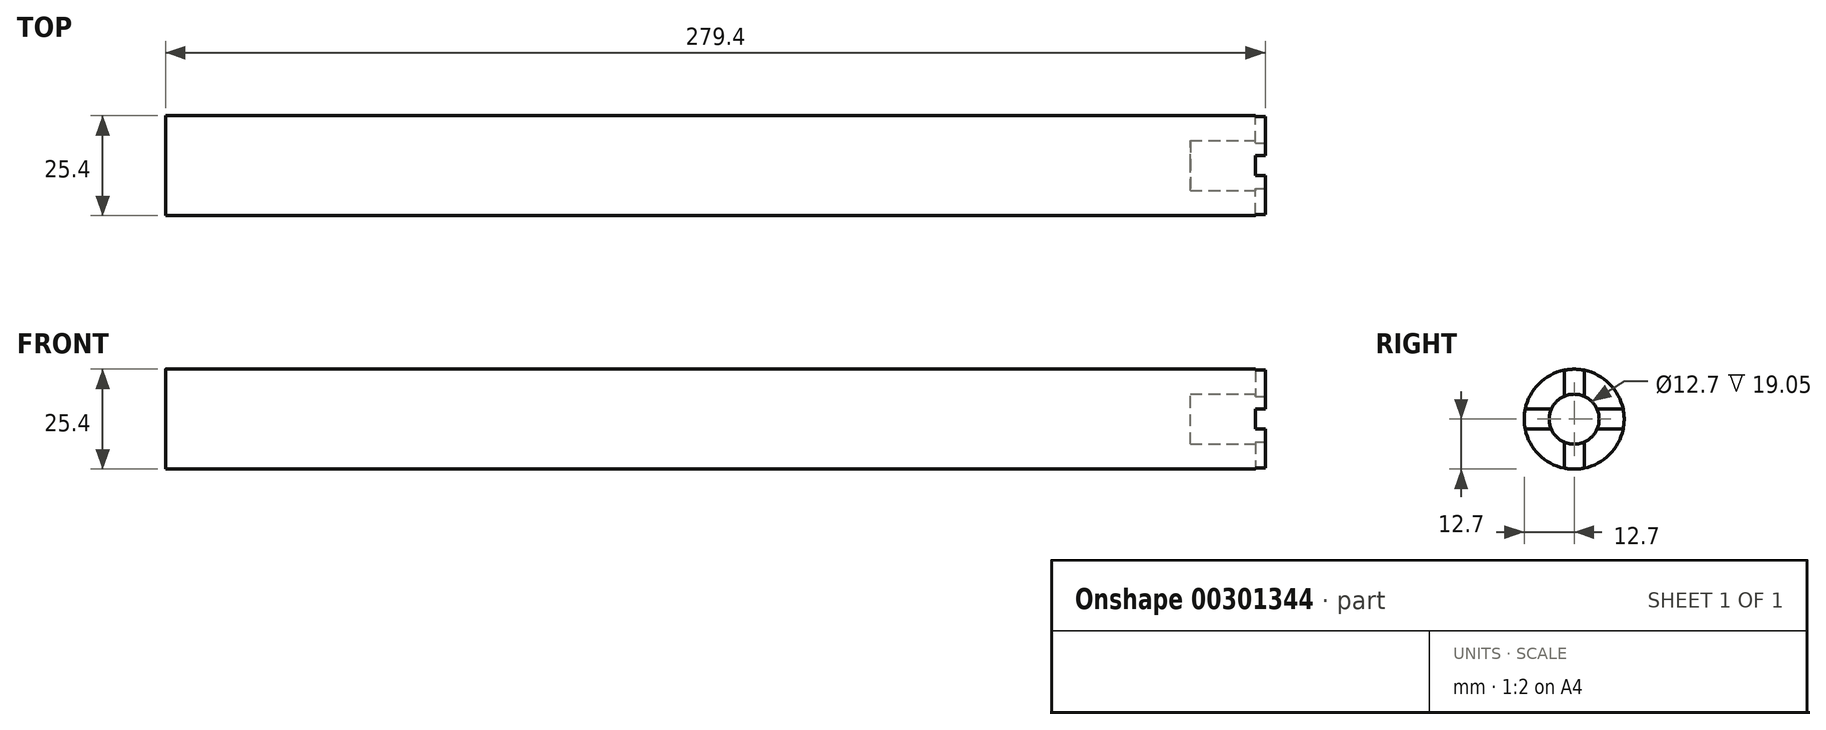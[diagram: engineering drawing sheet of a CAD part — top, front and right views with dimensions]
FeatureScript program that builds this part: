
annotation { "Feature Type Name" : "Feature", "Feature Type Description" : "" }
export const myFeature = defineFeature(function(context is Context, id is Id, definition is map)
    precondition{}
    {
        {
            var Q0;
            Q0=qCreatedBy(makeId("Right.planeOp"),FACE);
            var sketch = newSketch(context, id + "F0", { "sketchPlane" : qUnion([Q0])});
            skCircle(sketch, "E0", {"center": v(0, 0) * mm, "radius": 12.7 * mm});
            skSolve(sketch);
        }
        {
            var Q0;
            Q0 = qSketchRegion(id + "F0", true);
            extrude(context, id + "F1", {"entities" : qUnion([Q0]), "depth" : 279.4 * mm});
        }
        {
            var Q0;
            Q0=makeQuery(id+"F1.opExtrude","CAP_FACE",FACE,{"disambiguationData":[OSD([sQuery(id+"F0.wireOp",EDGE,"E0")])],"isStart":false});
            var sketch = newSketch(context, id + "F2", { "sketchPlane" : qUnion([Q0])});
            skCircle(sketch, "E1", {"center": v(0, 0) * mm, "radius": 6.35 * mm});
            skSolve(sketch);
        }
        {
            var Q0;
            Q0 = qSketchRegion(id + "F2", true);
            extrude(context, id + "F3", {"entities" : qUnion([Q0]), "operationType" : NewBodyOperationType.REMOVE, "oppositeDirection" : true, "depth" : 2.54 * mm});
        }
        {
            var Q0;
            Q0 = qSketchRegion(id + "F2", true);
            extrude(context, id + "F4", {"entities" : qUnion([Q0]), "operationType" : NewBodyOperationType.REMOVE, "oppositeDirection" : true, "depth" : 19.05 * mm});
        }
        {
            var Q0;
            Q0=makeQuery(id+"F1.opExtrude","CAP_FACE",FACE,{"disambiguationData":[OSD([sQuery(id+"F0.wireOp",EDGE,"E0")])],"isStart":false});
            var sketch = newSketch(context, id + "F5", { "sketchPlane" : qUnion([Q0])});
            skLineSegment(sketch, "E2.bottom", {"start": v(-20.7, 2.54) * mm, "end": v(27.3, 2.54) * mm});
            skLineSegment(sketch, "E2.top", {"start": v(-20.7, -2.54) * mm, "end": v(27.3, -2.54) * mm});
            skLineSegment(sketch, "E2.left", {"start": v(-20.7, 2.54) * mm, "end": v(-20.7, -2.54) * mm});
            skLineSegment(sketch, "E2.right", {"start": v(27.3, 2.54) * mm, "end": v(27.3, -2.54) * mm});
            skLineSegment(sketch, "E3.bottom", {"start": v(-2.54, 21.7) * mm, "end": v(2.54, 21.7) * mm});
            skLineSegment(sketch, "E3.top", {"start": v(-2.54, -24.63) * mm, "end": v(2.54, -24.63) * mm});
            skLineSegment(sketch, "E3.left", {"start": v(-2.54, 21.7) * mm, "end": v(-2.54, -24.63) * mm});
            skLineSegment(sketch, "E3.right", {"start": v(2.54, 21.7) * mm, "end": v(2.54, -24.63) * mm});
            skLineSegment(sketch, "E4", {"start": v(0, 0) * mm, "end": v(0, 8.96) * mm, "construction": true});
            skLineSegment(sketch, "E5", {"start": v(0, 0) * mm, "end": v(12.7, 0) * mm, "construction": true});
            skSolve(sketch);
        }
        {
            var Q0;
            Q0 = qSketchRegion(id + "F5", true);
            extrude(context, id + "F6", {"entities" : qUnion([Q0]), "operationType" : NewBodyOperationType.REMOVE, "oppositeDirection" : true, "depth" : 2.54 * mm});
        }
    });
